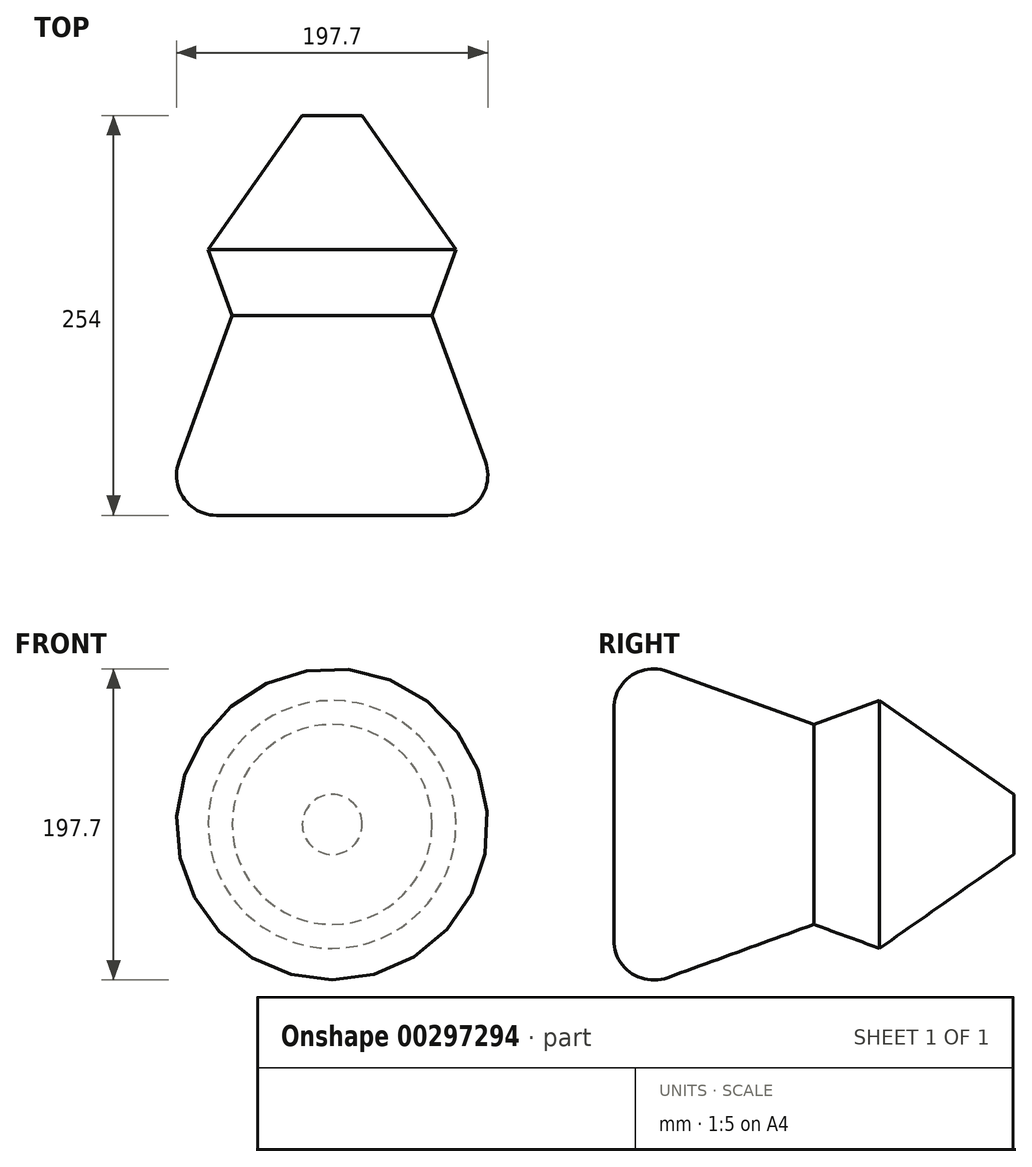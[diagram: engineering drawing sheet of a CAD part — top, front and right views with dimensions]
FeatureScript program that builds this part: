
annotation { "Feature Type Name" : "Feature", "Feature Type Description" : "" }
export const myFeature = defineFeature(function(context is Context, id is Id, definition is map)
    precondition{}
    {
        {
            var Q0;
            Q0=qCreatedBy(makeId("Front.planeOp"),FACE);
            var sketch = newSketch(context, id + "F0", { "sketchPlane" : qUnion([Q0])});
            skCircle(sketch, "E0", {"center": v(0, 0) * mm, "radius": 63.5 * mm});
            skSolve(sketch);
        }
        {
            var Q0;
            Q0=makeQuery(id+"F0.imprint","IMPRINT",FACE,{"disambiguationData":[TD([[makeQuery(id+"F0.imprint","IMPRINT",EDGE,{"derivedFrom":sQuery(id+"F0.wireOp",EDGE,"E0")}),1.0]])]});
            extrude(context, id + "F1", {"entities" : qUnion([Q0]), "endBound" : BoundingType.SYMMETRIC, "depth" : 254 * mm, "hasDraft" : true, "draftAngle" : 20 * degree});
        }
        {
            var Q0;
            Q0=makeQuery(id+"F1.opExtrude","CAP_EDGE",EDGE,{"disambiguationData":[OSD([sQuery(id+"F0.wireOp",EDGE,"E0")])],"isStart":true});
            chamfer(context, id + "F2", {"entities" : qUnion([Q0]), "width" : 63.5 * mm, "tangentPropagation" : true});
        }
        {
            var Q0;
            Q0=makeQuery(id+"F1.opExtrude","CAP_EDGE",EDGE,{"disambiguationData":[OSD([sQuery(id+"F0.wireOp",EDGE,"E0")])],"isStart":false});
            fillet(context, id + "F3", {"entities" : qUnion([Q0]), "radius" : 25.4 * mm, "tangentPropagation" : true, "allowEdgeOverflow" : false});
        }
    });
